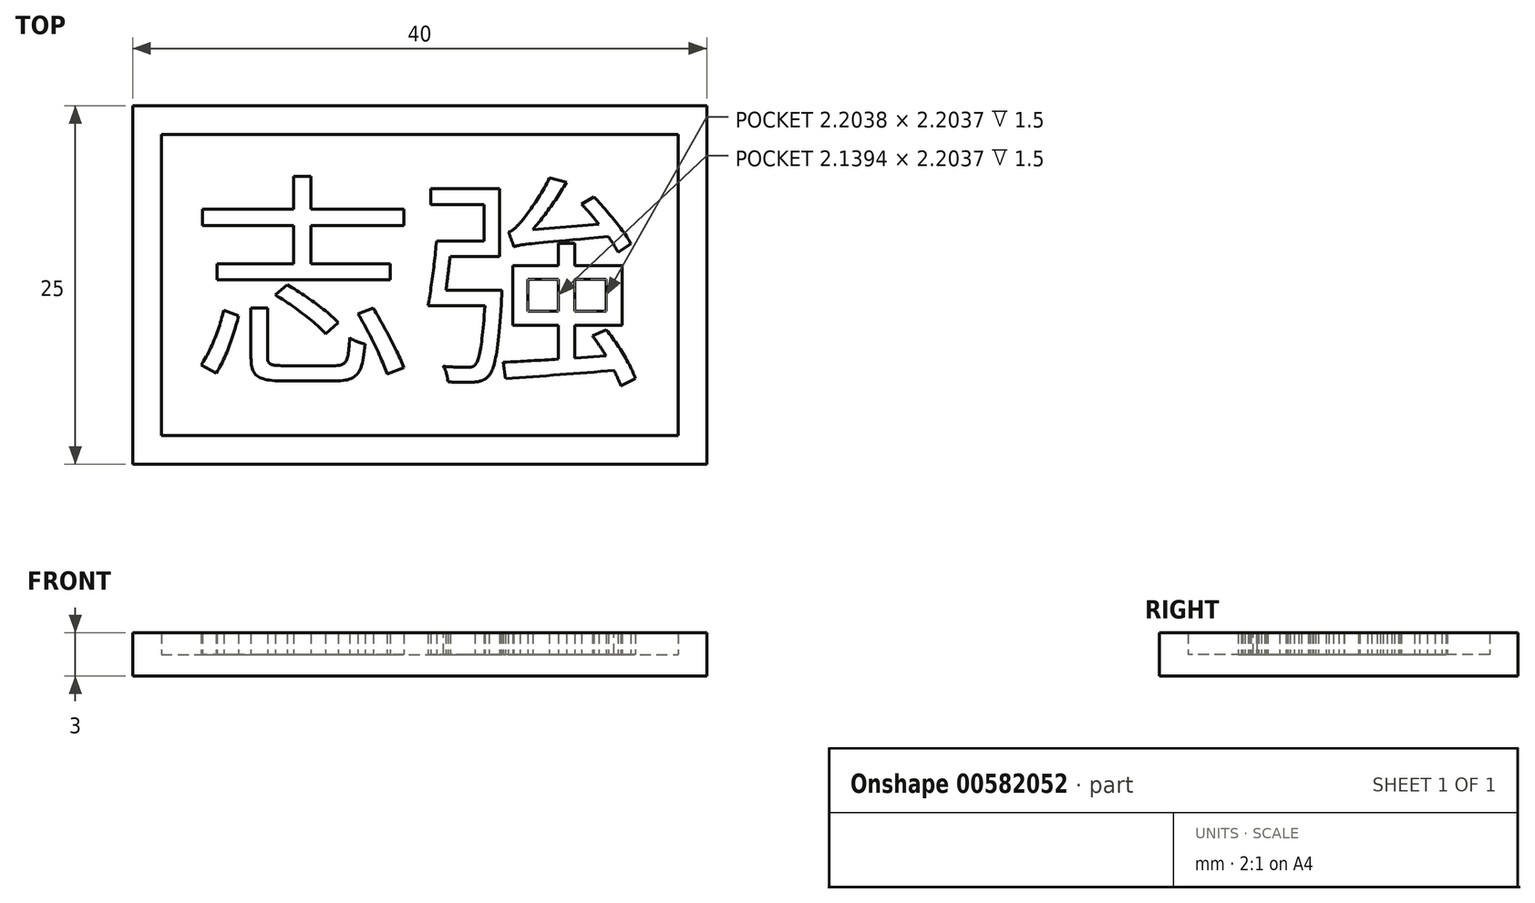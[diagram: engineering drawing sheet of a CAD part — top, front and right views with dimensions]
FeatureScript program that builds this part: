
annotation { "Feature Type Name" : "Feature", "Feature Type Description" : "" }
export const myFeature = defineFeature(function(context is Context, id is Id, definition is map)
    precondition{}
    {
        {
            var Q0;
            Q0=qCreatedBy(makeId("Top.planeOp"),FACE);
            var sketch = newSketch(context, id + "F0", { "sketchPlane" : qUnion([Q0])});
            skLineSegment(sketch, "E0.bottom", {"start": v(-20, 12.5) * mm, "end": v(20, 12.5) * mm});
            skLineSegment(sketch, "E0.top", {"start": v(-20, -12.5) * mm, "end": v(20, -12.5) * mm});
            skLineSegment(sketch, "E0.left", {"start": v(-20, 12.5) * mm, "end": v(-20, -12.5) * mm});
            skLineSegment(sketch, "E0.right", {"start": v(20, 12.5) * mm, "end": v(20, -12.5) * mm});
            skPoint(sketch, "E0.middle", {"position": v(0, 0) * mm});
            skSolve(sketch);
        }
        {
            var Q0;
            Q0 = qSketchRegion(id + "F0", true);
            extrude(context, id + "F1", {"entities" : qUnion([Q0]), "depth" : 1.5 * mm, "offsetDistance" : 25 * mm});
        }
        {
            var Q0;
            Q0=makeQuery(id+"F1.opExtrude","CAP_FACE",FACE,{"disambiguationData":[OSD([sQuery(id+"F0.wireOp",EDGE,"E0.bottom"),sQuery(id+"F0.wireOp",EDGE,"E0.top"),sQuery(id+"F0.wireOp",EDGE,"E0.left"),sQuery(id+"F0.wireOp",EDGE,"E0.right")])],"isStart":false});
            var sketch = newSketch(context, id + "F2", { "sketchPlane" : qUnion([Q0])});
            skLineSegment(sketch, "E1.bottom", {"start": v(-20, 12.5) * mm, "end": v(20, 12.5) * mm});
            skLineSegment(sketch, "E1.top", {"start": v(-20, -12.5) * mm, "end": v(20, -12.5) * mm});
            skLineSegment(sketch, "E1.left", {"start": v(-20, 12.5) * mm, "end": v(-20, -12.5) * mm});
            skLineSegment(sketch, "E1.right", {"start": v(20, 12.5) * mm, "end": v(20, -12.5) * mm});
            skLineSegment(sketch, "E2.0", {"start": v(18, 10.5) * mm, "end": v(18, -10.5) * mm});
            skLineSegment(sketch, "E2.1", {"start": v(-18, 10.5) * mm, "end": v(18, 10.5) * mm});
            skLineSegment(sketch, "E2.2", {"start": v(-18, 10.5) * mm, "end": v(-18, -10.5) * mm});
            skLineSegment(sketch, "E2.3", {"start": v(-18, -10.5) * mm, "end": v(18, -10.5) * mm});
            skSolve(sketch);
        }
        {
            var Q0;
            Q0 = qSketchRegion(id + "F2", true);
            extrude(context, id + "F3", {"entities" : qUnion([Q0]), "operationType" : NewBodyOperationType.ADD, "depth" : 1.5 * mm, "offsetDistance" : 25 * mm});
        }
        {
            var Q0;
            Q0=makeQuery(id+"F1.opExtrude","CAP_FACE",FACE,{"disambiguationData":[OSD([sQuery(id+"F0.wireOp",EDGE,"E0.bottom"),sQuery(id+"F0.wireOp",EDGE,"E0.top"),sQuery(id+"F0.wireOp",EDGE,"E0.left"),sQuery(id+"F0.wireOp",EDGE,"E0.right")])],"isStart":false});
            var sketch = newSketch(context, id + "F4", { "sketchPlane" : qUnion([Q0])});
            skText(sketch, "E3", { "text": "志強", "fontName": "NotoSansCJKtc-Regular.otf"});
            skPoint(sketch, "E4", {"position": v(15.93, 0) * mm});
            const initialGuessF4  = {"E3": [-0.01607, -0.0057, 1, 0, 0.01141]};
            skSetInitialGuess(sketch, initialGuessF4);
            skSolve(sketch);
        }
        {
            var Q0;
            Q0 = qSketchRegion(id + "F4", true);
            extrude(context, id + "F5", {"entities" : qUnion([Q0]), "operationType" : NewBodyOperationType.ADD, "depth" : 1.5 * mm, "offsetDistance" : 25 * mm});
        }
    });
